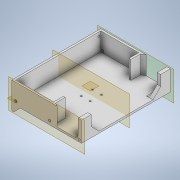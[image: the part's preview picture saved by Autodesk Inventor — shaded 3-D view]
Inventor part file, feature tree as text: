
AUTODESK INVENTOR PART (.ipt)
format: ipt  version: 2020 (Build 240168000, 168)  size: 308,736 bytes
history: native  units: mm
features: sketch x9, extrude x6, plane x6, rib x3, fillet x2, chamfer x1, hole x1, mirror x1
ambient origin geometry x8: Origin, YZ Plane, XZ Plane, XY Plane, X Axis, Y Axis, Z Axis, Center Point
bodies: Solid1 (feature_tree)
feature tree (29):
  extrude  "Extrusion1"  Depth=5.0mm
  extrude  "Extrusion2"  Depth=69.0mm
  extrude  "Extrusion3"  Depth=10.0mm
  extrude  "Extrusion4"  Depth=20.0mm
  chamfer  "Chamfer1"  [1 undecoded]
  fillet  "Fillet1"  Radius=5.0mm
  plane  "Work Plane3"
  plane  "Work Plane2"
  plane  "Work Plane4"
  extrude  "Extrusion8"  Depth=175.0mm TaperAngle=0.0deg
  extrude  "Extrusion9"  Depth=72.0mm
  hole  "Hole1"  [1 undecoded]
  plane  "Work Plane1"
  mirror  "Mirror1"
  plane  "Work Plane5"
  plane  "Work Plane6"
  sketch  "Sketch11"  dims[d23=5.0mm d24=72.0mm]
  sketch  "Sketch12"  dims[d25=5.0mm d33=25.0mm d34=20.594885mm]
  sketch  "Sketch13"  dims[d37=25.0mm d38=9.0mm d39=170.0mm d40=0.0mm d41=20.0mm d42=2.0mm d43=45.0deg d44=8.0mm d54=4.3mm d55=5.5mm d56=6.0mm d57=20.0mm d59=29.0mm d60=20.0mm d62=23.0mm d65=0.0mm d66=0.0mm d67=5.0mm d68=15.0mm d69=15.0mm d70=0.0mm d71=10.0mm d72=10.0mm d73=6.0mm d74=6.0mm d75=5.9mm d76=6.0mm d77=19.05mm d78=4.775mm d79=45.0deg d80=8.0mm d81=0.0mm d82=15.0mm d83=10.0mm d84=10.0mm d88=95.0mm d89=68.0mm d90=45.0deg d91=1.0mm d92=5.0mm d93=0.0mm d94=0.0mm d95=1.0mm d96=1.0mm d97=1.0mm d98=5.0mm d99=0.0mm d100=0.0mm d101=1.0mm d102=1.0mm d103=1.0mm d104=5.0mm d105=0.0mm d106=0.0mm d107=1.0mm d108=1.0mm d109=5.0mm]
  rib  "Rib1"
  rib  "Rib2"
  rib  "Rib3"
  fillet  "Fillet2"  Radius=20.594885mm
  sketch  "Sketch1"  dims[d0=230.0mm d1=5.0mm]
  sketch  "Sketch2"  dims[d2=69.0mm d3=0.0mm d4=5.3mm]
  sketch  "Sketch3"  dims[d5=10.0mm d6=10.0mm]
  sketch  "Sketch4"  dims[d7=20.0mm d9=210.0mm d10=20.0mm d12=49.0mm d15=95.0mm]
  sketch  "Sketch9"  dims[d16=20.0mm d17=0.0mm d18=0.0mm d19=5.0mm]
  sketch  "Sketch10"  dims[d20=7.0mm d21=175.0mm d22=0.0mm]
note: 2 required parameter values undecoded (feature->parameter linkage not recoverable at this tier; creation-order binding heuristic only, values carry confidence <= 0.55)
